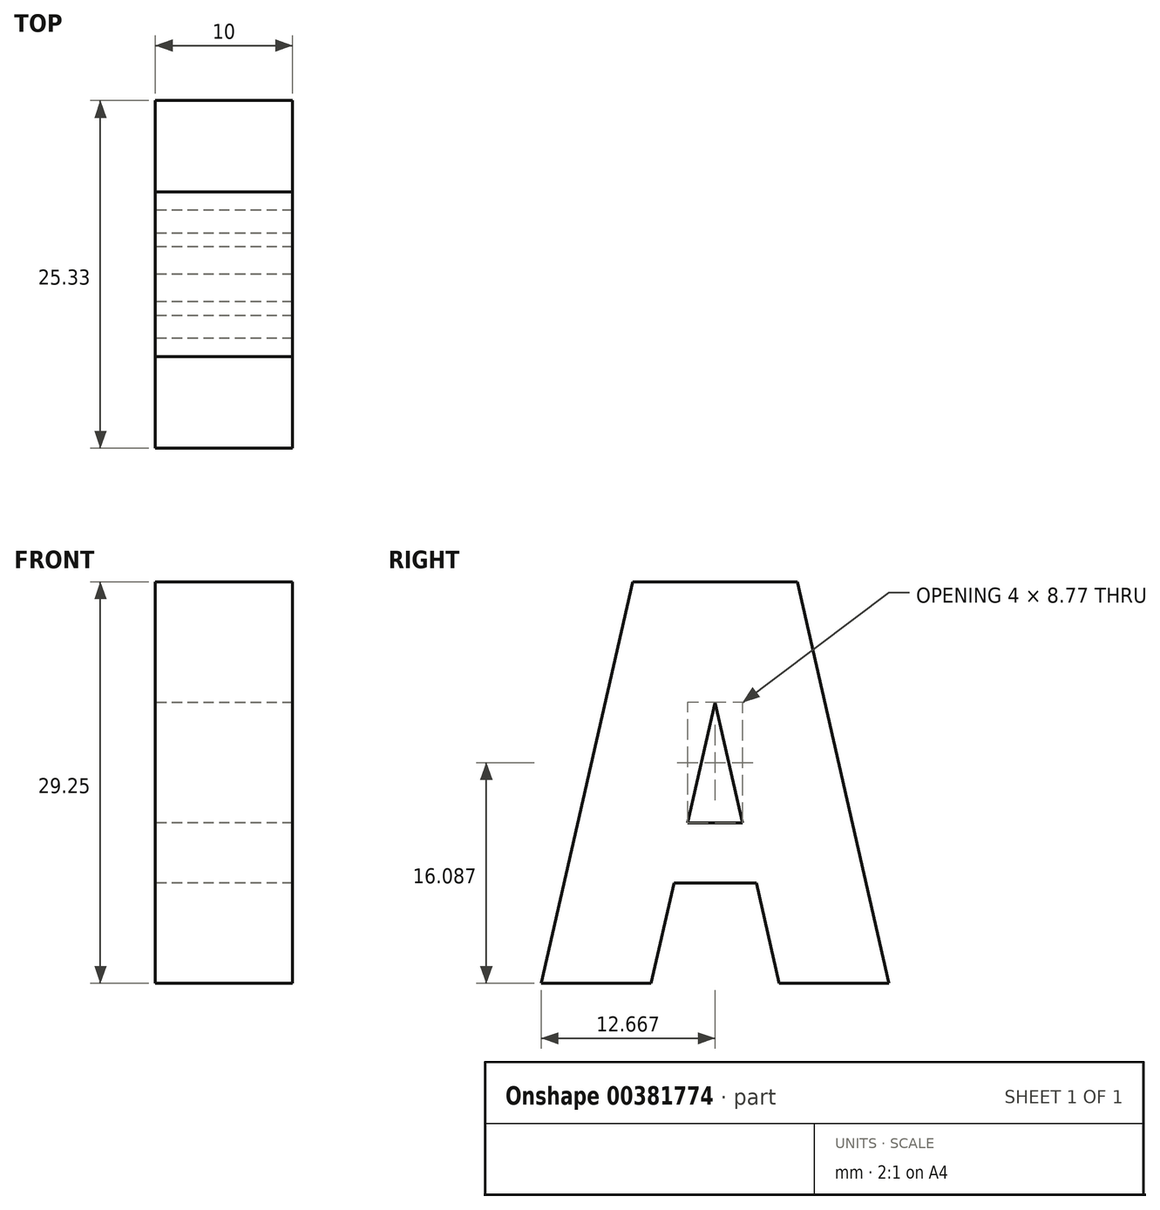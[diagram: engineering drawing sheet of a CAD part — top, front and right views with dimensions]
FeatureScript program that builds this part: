
annotation { "Feature Type Name" : "Feature", "Feature Type Description" : "" }
export const myFeature = defineFeature(function(context is Context, id is Id, definition is map)
    precondition{}
    {
        {
            var Q0;
            Q0=qCreatedBy(makeId("Right.planeOp"),FACE);
            var sketch = newSketch(context, id + "F0", { "sketchPlane" : qUnion([Q0])});
            skLineSegment(sketch, "E0", {"start": v(0, 0) * mm, "end": v(6.67, 29.25) * mm});
            skLineSegment(sketch, "E1", {"start": v(6.67, 29.25) * mm, "end": v(12.67, 29.25) * mm});
            skLineSegment(sketch, "E2", {"start": v(12.67, 29.25) * mm, "end": v(12.67, 0) * mm});
            skLineSegment(sketch, "E3", {"start": v(0, 0) * mm, "end": v(8, 0) * mm});
            skPoint(sketch, "E4.endSnap0", {"position": v(4, 0) * mm});
            skLineSegment(sketch, "E5", {"start": v(8, 0) * mm, "end": v(12.67, 20.47) * mm});
            skLineSegment(sketch, "E6", {"start": v(10.67, 11.7) * mm, "end": v(12.67, 11.7) * mm});
            skLineSegment(sketch, "E7", {"start": v(9.67, 7.31) * mm, "end": v(12.67, 7.31) * mm});
            skLineSegment(sketch, "E8", {"start": v(12.8, 29.31) * mm, "end": v(18.8, 29.31) * mm});
            skSolve(sketch);
        }
        {
            var Q0;
            Q0=makeQuery(id+"F0.imprint","IMPRINT",FACE,{"disambiguationData":[TD([[makeQuery(id+"F0.imprint","IMPRINT",EDGE,{"derivedFrom":sQuery(id+"F0.wireOp",EDGE,"E0")}),-1.0]])]});
            var Q1;
            {var subQ0=sQuery(id+"F0.wireOp",EDGE,"E6");Q1=makeQuery(id+"F0.imprint","IMPRINT",FACE,{"disambiguationData":[TD([[makeQuery(id+"F0.imprint","IMPRINT",EDGE,{"derivedFrom":subQ0}),-1.0]])]});}
            extrude(context, id + "F1", {"entities" : qUnion([Q0, Q1]), "depth" : 10 * mm});
        }
        {
            var Q0;
            Q0=makeQuery(id+"F1.opExtrude","SWEPT_BODY",BODY,{"disambiguationData":[OSD([sQuery(id+"F0.wireOp",EDGE,"E0"),sQuery(id+"F0.wireOp",EDGE,"E1"),sQuery(id+"F0.wireOp",EDGE,"E2"),sQuery(id+"F0.wireOp",EDGE,"E3"),sQuery(id+"F0.wireOp",EDGE,"E5"),sQuery(id+"F0.wireOp",EDGE,"E6"),sQuery(id+"F0.wireOp",EDGE,"E7")])]});
            var Q1;
            {var subQ0=sQuery(id+"F0.wireOp",EDGE,"E2");Q1=makeQuery(id+"F1.opExtrude","SWEPT_FACE",FACE,{"disambiguationData":[OSD([subQ0]),TDD([makeQuery(id+"F0.imprint","IMPRINT",EDGE,{"disambiguationData":[TD([[makeQuery(id+"F0.imprint","INTERSECT",VERTEX,{"derivedFrom":[sQuery(id+"F0.wireOp",EDGE,"E1"),subQ0]}),-1.0]])],"derivedFrom":subQ0})])]});}
            mirror(context, id + "F2", {"operationType" : NewBodyOperationType.ADD, "entities" : qUnion([Q0]), "mirrorPlane" : qUnion([Q1])});
        }
    });
